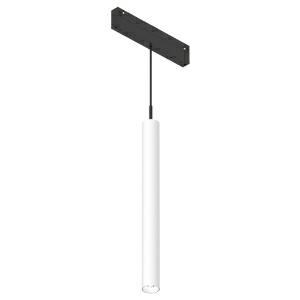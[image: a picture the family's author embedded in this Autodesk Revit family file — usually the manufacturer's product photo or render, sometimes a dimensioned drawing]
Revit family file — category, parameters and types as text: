
# Revit family: 2look4_25_magtrack_hangover_plug_o30_l300_insert_led_7w__2700k__48v__cri90_810-0423_2944
name_source: partatom
category: Leuchten
revit_build: Autodesk Revit 2016 (Build: 20190508_0715(x64)
units: mm (PartAtom-declared; Revit-internal decimal feet)

## family parameters
Basisbauteil = Fläche
Beim Laden mit Abzugskörper schneiden = Nein
Bemaßung runder Anschluss = Durchmesser verwenden
Gemeinsam genutzt = Nein
Lichtquelle = Nein
Raumberechnungspunkt = Nein
Teiletyp = Normal

## types (1)
- 810-0423-K24 (1 x LED, 448.11 lm, 6.4 W, 2700K)
    Beschreibung = The spot-insert 2LOOK4 25 MAGTRACK / 2LOOK4 50 MAGTRACK / HYPRO from the familiy 2LOOK4 consists of aluminum. The ballast is integrated and allows for an operation with 48V. 2LOOK4 25 MAGTRACK / 2LOOK4 50 MAGTRACK / HYPRO (# 810-0423) ist not dimmable (on/off). The lens based solution shows clear limits and creates sharp contours.
    CIE Flux Codes = 99 100 100 100 74
    Color Rendering = 1A/90…99
    Color Temperature = 2700K
    Height = 0 mm  [stored 0 ft]
    Hersteller = Prolicht
    Lamp Light Flux = 448.11 lm
    Lamp Power = 6.4 W
    Lamp count = 1
    Lampe = 1 x LED
    Length = 28 mm
    Luminous efficacy = 52 lm/W
    ModVariant = Nein
    Modell = 810-0423
    Mounting Place = Ceiling
    Mounting Type = Recessed
    Number of Poles = 1
    OnlyDefault = Ja
    Power Factor = 1
    Product Name = 2LOOK4 25 MAGTRACK__HANGOVER PLUG Ø30 L300 insert LED 7W  2700K  48V  CRI90
    Product group = Trimless recessed profile systems
    ProductGroupID = 414
    Protection Class = Protection class
    Protection Degree = Degree of protection
    RLX_Detail_Level = 1
    RlxData = <blob elided: 38593 chars, md5=ec17ee7a>
    Scheinlast = 6 VA
    Socket = socket
    Standby Power = 0 W
    System Light Flux = 331 lm
    System Power = 6 W
    Typenbild = 810-0423.jpg
    URL = http://relux.com
    VarID = 810-0423-k24
    Voltage = 0 V
    Vorgabe-Ansicht = 1800 mm
    Weight = 0.00 kg
    Width = 0 mm  [stored 0 ft]

note: [stored X ft] marks values corroborated as IEEE doubles in the binary element streams (Revit-internal decimal feet)

## geometry (parser evidence)
native form markers: Sweep x12
no freeform markers — native parametric forms only
